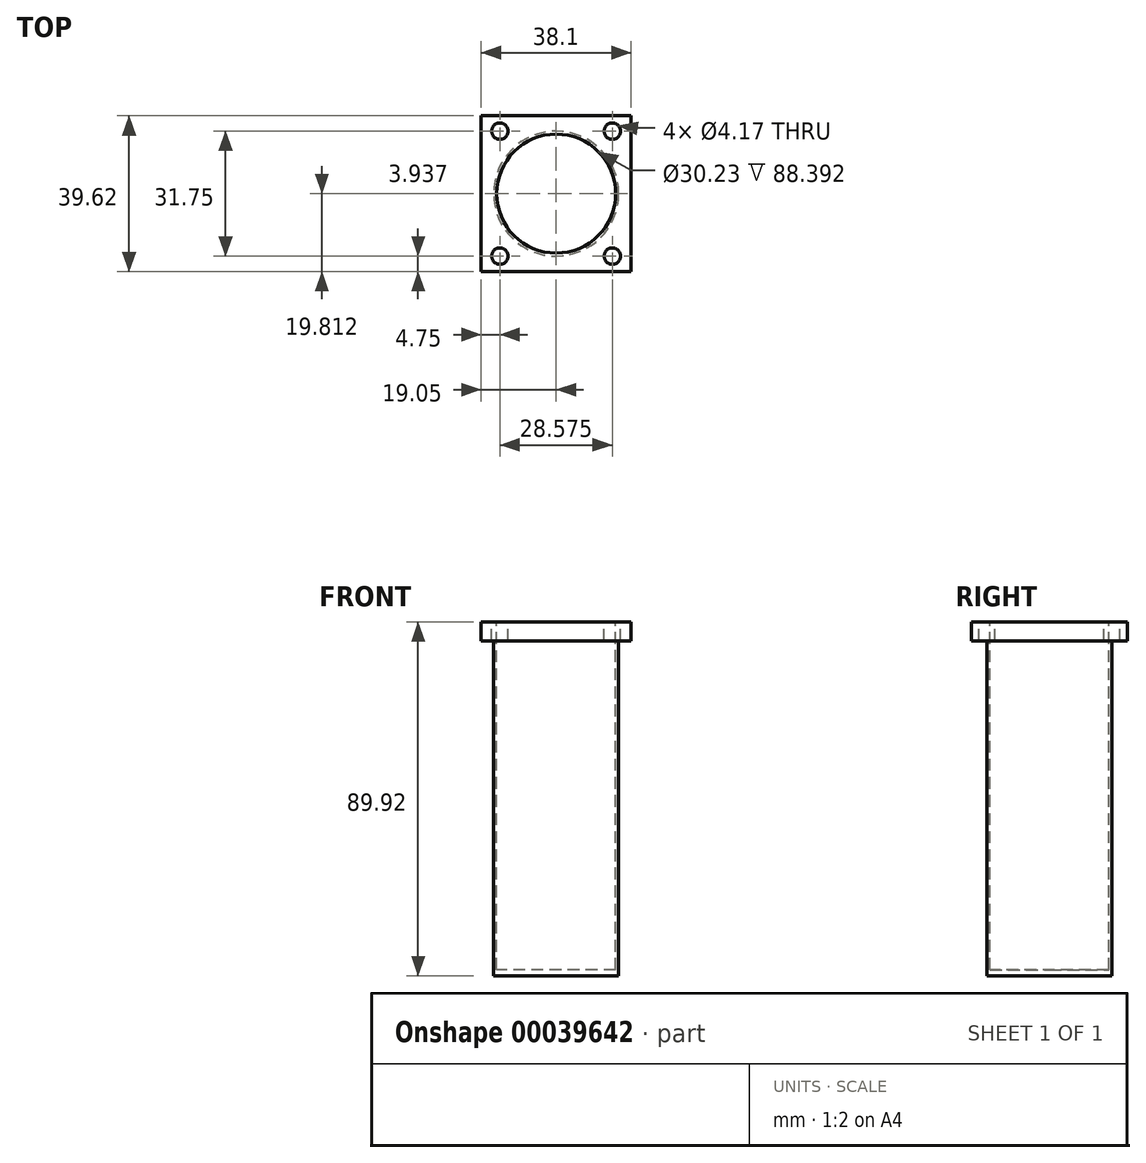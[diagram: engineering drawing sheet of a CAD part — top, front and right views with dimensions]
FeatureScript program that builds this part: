
annotation { "Feature Type Name" : "Feature", "Feature Type Description" : "" }
export const myFeature = defineFeature(function(context is Context, id is Id, definition is map)
    precondition{}
    {
        {
            var Q0;
            Q0=qCreatedBy(makeId("Top.planeOp"),FACE);
            var sketch = newSketch(context, id + "F0", { "sketchPlane" : qUnion([Q0])});
            skLineSegment(sketch, "E0.bottom", {"start": v(0, 39.62) * mm, "end": v(38.1, 39.62) * mm});
            skLineSegment(sketch, "E0.top", {"start": v(0, 0) * mm, "end": v(38.1, 0) * mm});
            skLineSegment(sketch, "E0.left", {"start": v(0, 39.62) * mm, "end": v(0, 0) * mm});
            skLineSegment(sketch, "E0.right", {"start": v(38.1, 39.62) * mm, "end": v(38.1, 0) * mm});
            skSolve(sketch);
        }
        {
            var Q0;
            Q0 = qSketchRegion(id + "F0", true);
            extrude(context, id + "F1", {"entities" : qUnion([Q0]), "oppositeDirection" : true, "depth" : 4.83 * mm});
        }
        {
            var Q0;
            Q0=makeQuery(id+"F1.opExtrude","CAP_FACE",FACE,{"disambiguationData":[OSD([sQuery(id+"F0.wireOp",EDGE,"E0.bottom"),sQuery(id+"F0.wireOp",EDGE,"E0.top"),sQuery(id+"F0.wireOp",EDGE,"E0.left"),sQuery(id+"F0.wireOp",EDGE,"E0.right")])],"isStart":true});
            var sketch = newSketch(context, id + "F2", { "sketchPlane" : qUnion([Q0])});
            skLineSegment(sketch, "E1", {"start": v(19.05, 39.62) * mm, "end": v(19.05, 0) * mm, "construction": true});
            skLineSegment(sketch, "E2", {"start": v(0, 19.81) * mm, "end": v(38.1, 19.81) * mm, "construction": true});
            skCircle(sketch, "E3", {"center": v(19.05, 19.81) * mm, "radius": 15.88 * mm});
            skSolve(sketch);
        }
        {
            var Q0;
            Q0 = qSketchRegion(id + "F2", true);
            extrude(context, id + "F3", {"entities" : qUnion([Q0]), "operationType" : NewBodyOperationType.ADD, "oppositeDirection" : true, "depth" : 89.92 * mm});
        }
        {
            var Q0;
            Q0=makeQuery(id+"F1.opExtrude","CAP_FACE",FACE,{"disambiguationData":[OSD([sQuery(id+"F0.wireOp",EDGE,"E0.bottom"),sQuery(id+"F0.wireOp",EDGE,"E0.top"),sQuery(id+"F0.wireOp",EDGE,"E0.left"),sQuery(id+"F0.wireOp",EDGE,"E0.right")])],"isStart":true});
            var sketch = newSketch(context, id + "F4", { "sketchPlane" : qUnion([Q0])});
            skLineSegment(sketch, "E4", {"start": v(19.05, 39.62) * mm, "end": v(19.05, 0) * mm, "construction": true});
            skLineSegment(sketch, "E5", {"start": v(0, 19.81) * mm, "end": v(38.1, 19.81) * mm, "construction": true});
            skCircle(sketch, "E6", {"center": v(19.05, 19.81) * mm, "radius": 15.11 * mm});
            skSolve(sketch);
        }
        {
            var Q0;
            Q0 = qSketchRegion(id + "F4", true);
            extrude(context, id + "F5", {"entities" : qUnion([Q0]), "operationType" : NewBodyOperationType.REMOVE, "oppositeDirection" : true, "depth" : 88.4 * mm});
        }
        {
            var Q0;
            Q0=qCreatedBy(makeId("Top.planeOp"),FACE);
            var sketch = newSketch(context, id + "F6", { "sketchPlane" : qUnion([Q0])});
            skCircle(sketch, "E7", {"center": v(33.32, 35.69) * mm, "radius": 2.08 * mm});
            skCircle(sketch, "E8.0.1.0", {"center": v(33.32, 3.94) * mm, "radius": 2.08 * mm});
            skCircle(sketch, "E8.1.0.0", {"center": v(4.75, 35.69) * mm, "radius": 2.08 * mm});
            skCircle(sketch, "E8.1.1.0", {"center": v(4.75, 3.94) * mm, "radius": 2.08 * mm});
            skLineSegment(sketch, "E8.direction1", {"start": v(33.32, 35.69) * mm, "end": v(4.75, 35.69) * mm, "construction": true});
            skLineSegment(sketch, "E8.direction2", {"start": v(33.32, 35.69) * mm, "end": v(33.32, 3.94) * mm, "construction": true});
            skSolve(sketch);
        }
        {
            var Q0;
            Q0 = qSketchRegion(id + "F6", true);
            extrude(context, id + "F7", {"entities" : qUnion([Q0]), "operationType" : NewBodyOperationType.REMOVE, "endBound" : BoundingType.THROUGH_ALL, "oppositeDirection" : true, "depth" : 25.4 * mm});
        }
    });
